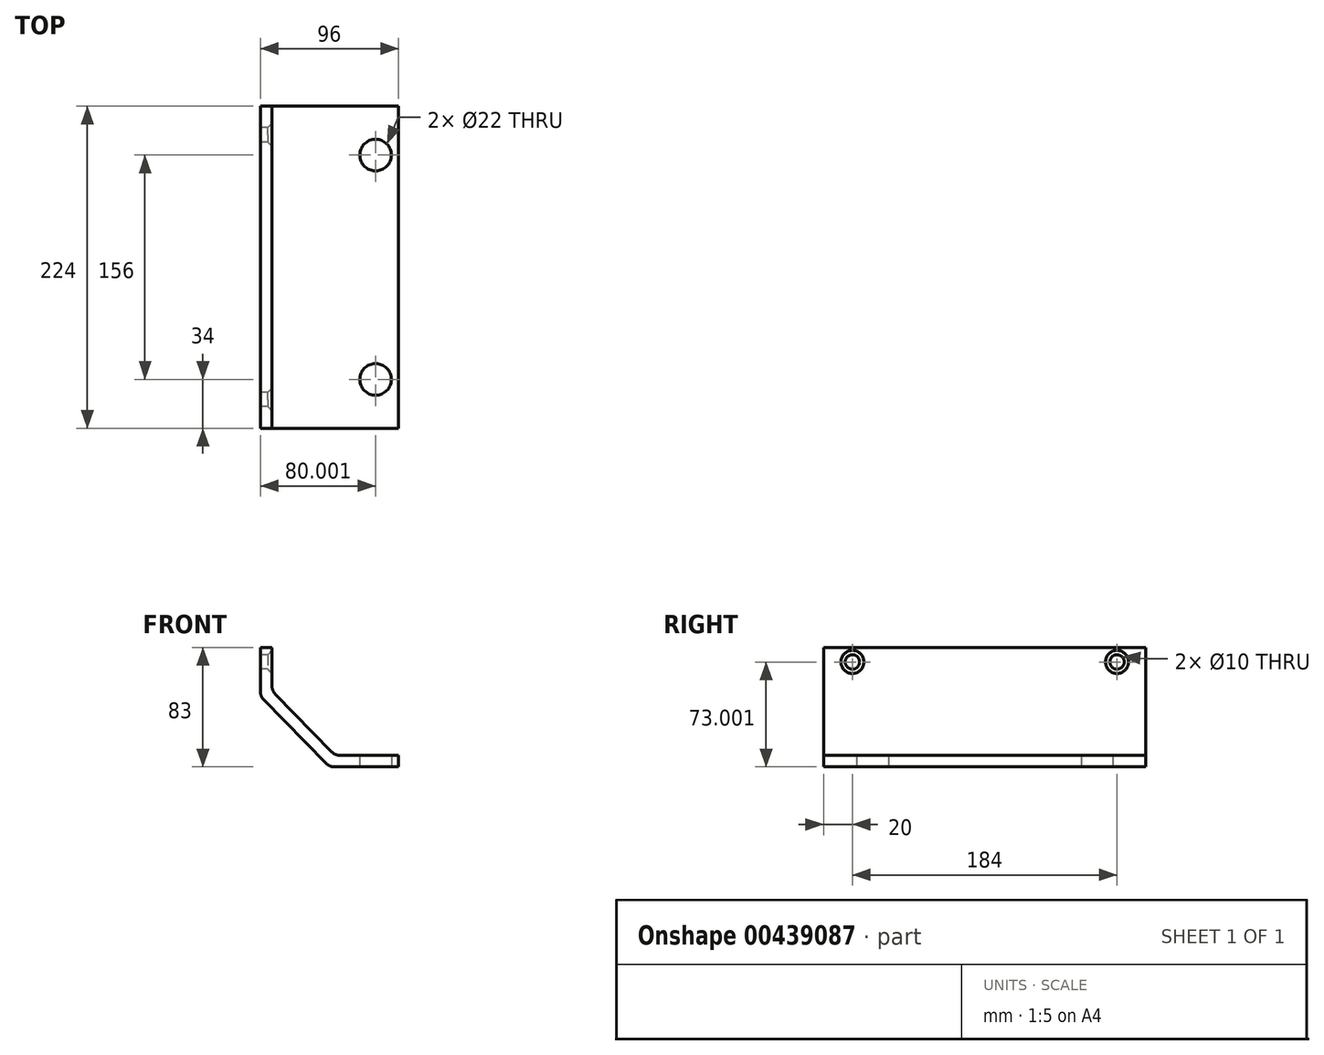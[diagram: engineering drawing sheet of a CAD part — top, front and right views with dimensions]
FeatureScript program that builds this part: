
annotation { "Feature Type Name" : "Feature", "Feature Type Description" : "" }
export const myFeature = defineFeature(function(context is Context, id is Id, definition is map)
    precondition{}
    {
        {
            var Q0;
            Q0=qCreatedBy(makeId("Front.planeOp"),FACE);
            var sketch = newSketch(context, id + "F0", { "sketchPlane" : qUnion([Q0])});
            skLineSegment(sketch, "E0.bottom", {"start": v(-24.86, 54.17) * mm, "end": v(-16.86, 54.17) * mm});
            skLineSegment(sketch, "E0.top", {"start": v(-24.86, 24.17) * mm, "end": v(-16.86, 24.17) * mm});
            skLineSegment(sketch, "E0.left", {"start": v(-24.86, 54.17) * mm, "end": v(-24.86, 24.17) * mm});
            skLineSegment(sketch, "E0.right", {"start": v(-16.86, 54.17) * mm, "end": v(-16.86, 24.17) * mm});
            skLineSegment(sketch, "E1.left", {"start": v(-24.86, 24.17) * mm, "end": v(-24.86, 20.17) * mm});
            skLineSegment(sketch, "E2", {"start": v(-24.86, 20.17) * mm, "end": v(-16.86, 24.17) * mm});
            skLineSegment(sketch, "E3.bottom", {"start": v(27.14, -20.83) * mm, "end": v(71.14, -20.83) * mm});
            skLineSegment(sketch, "E3.top", {"start": v(27.14, -28.83) * mm, "end": v(71.14, -28.83) * mm});
            skLineSegment(sketch, "E3.left", {"start": v(27.14, -20.83) * mm, "end": v(27.14, -28.83) * mm});
            skLineSegment(sketch, "E3.right", {"start": v(71.14, -20.83) * mm, "end": v(71.14, -28.83) * mm});
            skLineSegment(sketch, "E4.top", {"start": v(27.14, -28.83) * mm, "end": v(23.14, -28.83) * mm});
            skLineSegment(sketch, "E5", {"start": v(23.14, -28.83) * mm, "end": v(27.14, -20.83) * mm});
            skLineSegment(sketch, "E6", {"start": v(-24.86, 20.17) * mm, "end": v(23.14, -28.83) * mm});
            skLineSegment(sketch, "E7", {"start": v(-16.86, 24.17) * mm, "end": v(27.14, -20.83) * mm});
            skSolve(sketch);
        }
        {
            var Q0;
            Q0=qSketchRegion(id+"F0",true);
            extrude(context, id + "F1", {"entities" : qUnion([Q0]), "depth" : 224 * mm});
        }
        {
            var Q0;
            Q0=makeQuery(id+"F1.opExtrude","SWEPT_FACE",FACE,{"disambiguationData":[OSD([sQuery(id+"F0.wireOp",EDGE,"E0.left"),sQuery(id+"F0.wireOp",EDGE,"E1.left")])]});
            var sketch = newSketch(context, id + "F2", { "sketchPlane" : qUnion([Q0])});
            skCircle(sketch, "E8", {"center": v(20, 44.17) * mm, "radius": 5 * mm});
            skCircle(sketch, "E9", {"center": v(204, 44.17) * mm, "radius": 5 * mm});
            skSolve(sketch);
        }
        {
            var Q0;
            Q0 = qSketchRegion(id + "F2", true);
            extrude(context, id + "F3", {"entities" : qUnion([Q0]), "operationType" : NewBodyOperationType.REMOVE, "oppositeDirection" : true, "depth" : 25 * mm});
        }
        {
            var Q0;
            Q0=makeQuery(id+"F1.opExtrude","SWEPT_FACE",FACE,{"disambiguationData":[OSD([sQuery(id+"F0.wireOp",EDGE,"E3.top"),sQuery(id+"F0.wireOp",EDGE,"E4.top")])]});
            var sketch = newSketch(context, id + "F4", { "sketchPlane" : qUnion([Q0])});
            skCircle(sketch, "E10", {"center": v(55.14, 34) * mm, "radius": 11 * mm});
            skCircle(sketch, "E11", {"center": v(55.14, 190) * mm, "radius": 11 * mm});
            skSolve(sketch);
        }
        {
            var Q0;
            Q0 = qSketchRegion(id + "F4", true);
            extrude(context, id + "F5", {"entities" : qUnion([Q0]), "operationType" : NewBodyOperationType.REMOVE, "oppositeDirection" : true, "depth" : 25 * mm});
        }
        {
            var Q0;
            Q0=makeQuery(id+"F3.boolean.opBoolean","INTERSECT",EDGE,{"derivedFrom":[makeQuery(id+"F1.opExtrude","SWEPT_FACE",FACE,{"disambiguationData":[OSD([sQuery(id+"F0.wireOp",EDGE,"E0.right")])]}),makeQuery(id+"F3.opExtrude","SWEPT_FACE",FACE,{"disambiguationData":[OSD([sQuery(id+"F2.wireOp",EDGE,"E9")])]})]});
            var Q1;
            Q1=makeQuery(id+"F3.boolean.opBoolean","INTERSECT",EDGE,{"derivedFrom":[makeQuery(id+"F1.opExtrude","SWEPT_FACE",FACE,{"disambiguationData":[OSD([sQuery(id+"F0.wireOp",EDGE,"E0.right")])]}),makeQuery(id+"F3.opExtrude","SWEPT_FACE",FACE,{"disambiguationData":[OSD([sQuery(id+"F2.wireOp",EDGE,"E8")])]})]});
            chamfer(context, id + "F6", {"entities" : qUnion([Q0, Q1]), "width" : 3 * mm, "tangentPropagation" : true});
        }
        {
            var Q0;
            Q0=makeQuery(id+"F1.opExtrude","SWEPT_EDGE",EDGE,{"disambiguationData":[OSD([sQuery(id+"F0.wireOp",EDGE,"E0.right"),sQuery(id+"F0.wireOp",EDGE,"E1.bottom"),sQuery(id+"F0.wireOp",EDGE,"E2"),sQuery(id+"F0.wireOp",EDGE,"E7")])]});
            var Q1;
            Q1=makeQuery(id+"F1.opExtrude","SWEPT_EDGE",EDGE,{"disambiguationData":[OSD([sQuery(id+"F0.wireOp",EDGE,"E3.bottom"),sQuery(id+"F0.wireOp",EDGE,"E3.left"),sQuery(id+"F0.wireOp",EDGE,"E5"),sQuery(id+"F0.wireOp",EDGE,"E7")])]});
            fillet(context, id + "F7", {"entities" : qUnion([Q0, Q1]), "radius" : 8 * mm, "tangentPropagation" : true, "allowEdgeOverflow" : false});
        }
        {
            var Q0;
            Q0=makeQuery(id+"F1.opExtrude","SWEPT_EDGE",EDGE,{"disambiguationData":[OSD([sQuery(id+"F0.wireOp",EDGE,"E1.left"),sQuery(id+"F0.wireOp",EDGE,"E2"),sQuery(id+"F0.wireOp",EDGE,"E6")])]});
            var Q1;
            Q1=makeQuery(id+"F1.opExtrude","SWEPT_EDGE",EDGE,{"disambiguationData":[OSD([sQuery(id+"F0.wireOp",EDGE,"E4.top"),sQuery(id+"F0.wireOp",EDGE,"E5"),sQuery(id+"F0.wireOp",EDGE,"E6")])]});
            fillet(context, id + "F8", {"entities" : qUnion([Q0, Q1]), "radius" : 8 * mm, "tangentPropagation" : true, "allowEdgeOverflow" : false});
        }
    });
